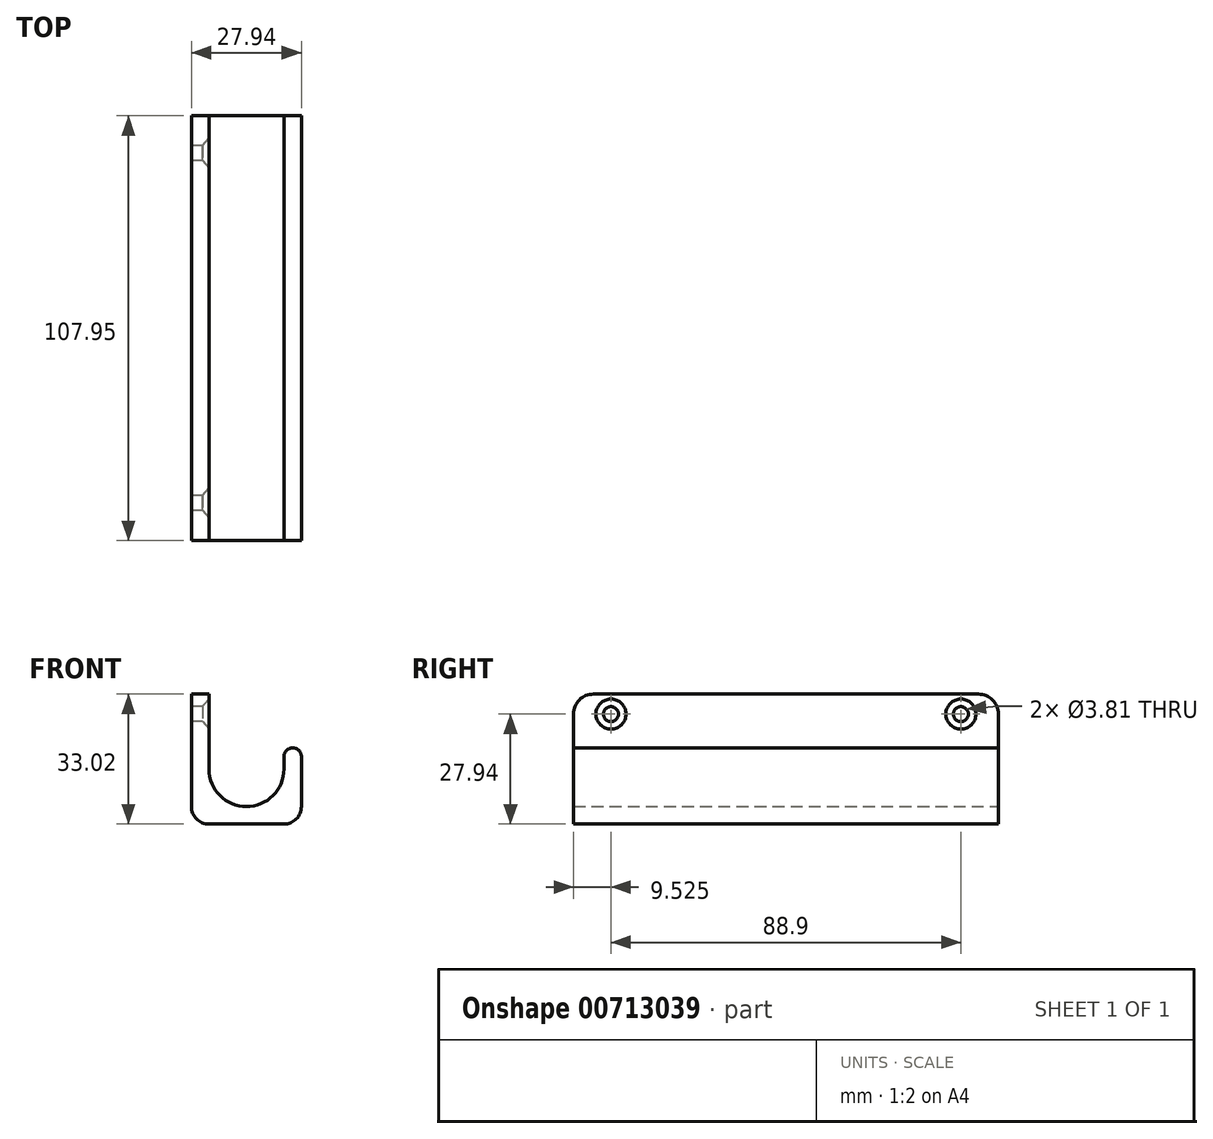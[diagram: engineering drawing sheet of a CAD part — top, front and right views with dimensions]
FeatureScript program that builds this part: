
annotation { "Feature Type Name" : "Feature", "Feature Type Description" : "" }
export const myFeature = defineFeature(function(context is Context, id is Id, definition is map)
    precondition{}
    {
        {
            var Q0;
            Q0=qCreatedBy(makeId("Front.planeOp"),FACE);
            var sketch = newSketch(context, id + "F0", { "sketchPlane" : qUnion([Q0])});
            skLineSegment(sketch, "E0", {"start": v(0, 0) * mm, "end": v(0, -28.57) * mm});
            skLineSegment(sketch, "E1", {"start": v(3.18, -31.75) * mm, "end": v(22.23, -31.75) * mm});
            skLineSegment(sketch, "E2", {"start": v(25.4, -28.57) * mm, "end": v(25.4, -15.87) * mm});
            skLineSegment(sketch, "E3", {"start": v(3.18, -19.05) * mm, "end": v(3.18, 0) * mm});
            skLineSegment(sketch, "E4", {"start": v(3.18, 0) * mm, "end": v(0, 0) * mm});
            skLineSegment(sketch, "E5", {"start": v(22.23, -15.87) * mm, "end": v(22.23, -19.05) * mm});
            skArc(sketch, "E6", {"start": v(3.18, -19.05) * mm, "mid": v(12.7, -28.58) * mm, "end": v(22.23, -19.05) * mm});
            skArc(sketch, "E7", {"start": v(22.23, -15.87) * mm, "mid": v(23.81, -14.29) * mm, "end": v(25.4, -15.87) * mm});
            skPoint(sketch, "E8.visualSharp", {"position": v(0, -31.75) * mm});
            skArc(sketch, "E8.filletArc", {"start": v(0, -28.57) * mm, "mid": v(0.93, -30.82) * mm, "end": v(3.18, -31.75) * mm});
            skPoint(sketch, "E9.visualSharp", {"position": v(25.4, -31.75) * mm});
            skArc(sketch, "E9.filletArc", {"start": v(22.23, -31.75) * mm, "mid": v(24.47, -30.82) * mm, "end": v(25.4, -28.57) * mm});
            skSolve(sketch);
        }
        {
            var Q0;
            Q0 = qSketchRegion(id + "F0", true);
            extrude(context, id + "F1", {"entities" : qUnion([Q0]), "depth" : 107.95 * mm, "offsetDistance" : 25.4 * mm});
        }
        {
            var Q0;
            Q0=makeQuery(id+"F1.opExtrude","SWEPT_FACE",FACE,{"disambiguationData":[OSD([sQuery(id+"F0.wireOp",EDGE,"E0")])]});
            var sketch = newSketch(context, id + "F2", { "sketchPlane" : qUnion([Q0])});
            skPoint(sketch, "E10.start.orphan", {"position": v(53.98, 0) * mm});
            skCircle(sketch, "E11", {"center": v(9.52, -5.08) * mm, "radius": 1.9 * mm});
            skCircle(sketch, "E12", {"center": v(98.43, -5.08) * mm, "radius": 1.9 * mm});
            skSolve(sketch);
        }
        {
            var Q0;
            Q0=makeQuery(id+"F1.opExtrude","CAP_EDGE",EDGE,{"disambiguationData":[OSD([sQuery(id+"F0.wireOp",EDGE,"E4")])],"isStart":true});
            var Q1;
            Q1=makeQuery(id+"F1.opExtrude","CAP_EDGE",EDGE,{"disambiguationData":[OSD([sQuery(id+"F0.wireOp",EDGE,"E4")])],"isStart":false});
            fillet(context, id + "F3", {"entities" : qUnion([Q0, Q1]), "radius" : 1.59 * mm, "tangentPropagation" : true, "allowEdgeOverflow" : false});
        }
        {
            var Q0;
            Q0 = qSketchRegion(id + "F2", true);
            extrude(context, id + "F4", {"entities" : qUnion([Q0]), "operationType" : NewBodyOperationType.REMOVE, "oppositeDirection" : true, "depth" : 25.4 * mm, "offsetDistance" : 25.4 * mm});
        }
        {
            var Q0;
            Q0=makeQuery(id+"F4.boolean.opBoolean","INTERSECT",EDGE,{"derivedFrom":[makeQuery(id+"F1.opExtrude","SWEPT_FACE",FACE,{"disambiguationData":[OSD([sQuery(id+"F0.wireOp",EDGE,"E3")])]}),makeQuery(id+"F4.opExtrude","SWEPT_FACE",FACE,{"disambiguationData":[OSD([sQuery(id+"F2.wireOp",EDGE,"E12")])]})]});
            var Q1;
            Q1=makeQuery(id+"F4.boolean.opBoolean","INTERSECT",EDGE,{"derivedFrom":[makeQuery(id+"F1.opExtrude","SWEPT_FACE",FACE,{"disambiguationData":[OSD([sQuery(id+"F0.wireOp",EDGE,"E3")])]}),makeQuery(id+"F4.opExtrude","SWEPT_FACE",FACE,{"disambiguationData":[OSD([sQuery(id+"F2.wireOp",EDGE,"E11")])]})]});
            chamfer(context, id + "F5", {"entities" : qUnion([Q0, Q1]), "chamferType" : ChamferType.OFFSET_ANGLE, "width" : 1.65 * mm, "oppositeDirection" : false, "angle" : 41 * degree, "tangentPropagation" : true});
        }
        {
            var Q0;
            Q0=makeQuery(id+"F1.opExtrude","CAP_FACE",FACE,{"disambiguationData":[OSD([sQuery(id+"F0.wireOp",EDGE,"E0"),sQuery(id+"F0.wireOp",EDGE,"E1"),sQuery(id+"F0.wireOp",EDGE,"E2"),sQuery(id+"F0.wireOp",EDGE,"E3"),sQuery(id+"F0.wireOp",EDGE,"E4"),sQuery(id+"F0.wireOp",EDGE,"E5"),sQuery(id+"F0.wireOp",EDGE,"E6"),sQuery(id+"F0.wireOp",EDGE,"E7"),sQuery(id+"F0.wireOp",EDGE,"E8.filletArc"),sQuery(id+"F0.wireOp",EDGE,"E9.filletArc")])],"isStart":false});
            var sketch = newSketch(context, id + "F6", { "sketchPlane" : qUnion([Q0])});
            skLineSegment(sketch, "E13.0", {"start": v(0, 0) * mm, "end": v(3.18, 0) * mm});
            skLineSegment(sketch, "E13.3", {"start": v(3.18, -19.05) * mm, "end": v(3.18, 0) * mm});
            skLineSegment(sketch, "E13.4", {"start": v(0, 0) * mm, "end": v(0, -28.57) * mm});
            skArc(sketch, "E13.5", {"start": v(3.18, -19.05) * mm, "mid": v(12.7, -28.58) * mm, "end": v(22.23, -19.05) * mm});
            skLineSegment(sketch, "E13.6", {"start": v(22.23, -15.87) * mm, "end": v(22.23, -19.05) * mm});
            skArc(sketch, "E13.7", {"start": v(22.23, -15.87) * mm, "mid": v(23.81, -14.29) * mm, "end": v(25.4, -15.87) * mm});
            skLineSegment(sketch, "E13.8", {"start": v(25.4, -28.57) * mm, "end": v(25.4, -15.87) * mm});
            skArc(sketch, "E13.9", {"start": v(22.23, -31.75) * mm, "mid": v(24.47, -30.82) * mm, "end": v(25.4, -28.57) * mm});
            skLineSegment(sketch, "E13.10", {"start": v(3.18, -31.75) * mm, "end": v(22.23, -31.75) * mm});
            skArc(sketch, "E13.11", {"start": v(0, -28.57) * mm, "mid": v(0.93, -30.82) * mm, "end": v(3.18, -31.75) * mm});
            skLineSegment(sketch, "E14.0", {"start": v(26.67, -28.57) * mm, "end": v(26.67, -15.87) * mm});
            skLineSegment(sketch, "E14.1", {"start": v(-1.27, 0) * mm, "end": v(-1.27, -28.57) * mm});
            skArc(sketch, "E14.2", {"start": v(-1.27, -28.57) * mm, "mid": v(0.03, -31.72) * mm, "end": v(3.18, -33.02) * mm});
            skLineSegment(sketch, "E14.3", {"start": v(3.18, -33.02) * mm, "end": v(22.23, -33.02) * mm});
            skArc(sketch, "E14.4", {"start": v(22.23, -33.02) * mm, "mid": v(25.37, -31.72) * mm, "end": v(26.67, -28.57) * mm});
            skArc(sketch, "E15", {"start": v(26.67, -15.87) * mm, "mid": v(24.45, -13.65) * mm, "end": v(22.23, -15.87) * mm});
            skLineSegment(sketch, "E16", {"start": v(-1.27, 0) * mm, "end": v(0, 0) * mm});
            skSolve(sketch);
        }
        {
            var Q0;
            Q0 = qSketchRegion(id + "F6", true);
            var Q1;
            Q1=makeQuery(id+"F1.opExtrude","CAP_FACE",FACE,{"disambiguationData":[OSD([sQuery(id+"F0.wireOp",EDGE,"E0"),sQuery(id+"F0.wireOp",EDGE,"E1"),sQuery(id+"F0.wireOp",EDGE,"E2"),sQuery(id+"F0.wireOp",EDGE,"E3"),sQuery(id+"F0.wireOp",EDGE,"E4"),sQuery(id+"F0.wireOp",EDGE,"E5"),sQuery(id+"F0.wireOp",EDGE,"E6"),sQuery(id+"F0.wireOp",EDGE,"E7"),sQuery(id+"F0.wireOp",EDGE,"E8.filletArc"),sQuery(id+"F0.wireOp",EDGE,"E9.filletArc")])],"isStart":true});
            extrude(context, id + "F7", {"entities" : qUnion([Q0]), "operationType" : NewBodyOperationType.ADD, "endBound" : BoundingType.UP_TO_SURFACE, "oppositeDirection" : true, "depth" : 25.4 * mm, "endBoundEntityFace" : qUnion([Q1]), "offsetDistance" : 25.4 * mm});
        }
        {
            var Q0;
            Q0=makeQuery(id+"F7.opExtrude","SWEPT_FACE",FACE,{"disambiguationData":[OSD([sQuery(id+"F6.wireOp",EDGE,"E14.1")])]});
            var sketch = newSketch(context, id + "F8", { "sketchPlane" : qUnion([Q0])});
            skPoint(sketch, "E17.0", {"position": v(53.98, 0) * mm});
            skCircle(sketch, "E17.1", {"center": v(9.52, -5.08) * mm, "radius": 1.9 * mm});
            skCircle(sketch, "E17.2", {"center": v(98.43, -5.08) * mm, "radius": 1.9 * mm});
            skSolve(sketch);
        }
        {
            var Q0;
            Q0 = qSketchRegion(id + "F8", true);
            extrude(context, id + "F9", {"entities" : qUnion([Q0]), "operationType" : NewBodyOperationType.REMOVE, "oppositeDirection" : true, "depth" : 25.4 * mm, "offsetDistance" : 25.4 * mm});
        }
        {
            var Q0;
            Q0=makeQuery(id+"F9.boolean.opBoolean","INTERSECT",EDGE,{"derivedFrom":[makeQuery(id+"F7.boolean.opBoolean","MERGE",FACE,{"derivedFrom":[makeQuery(id+"F1.opExtrude","SWEPT_FACE",FACE,{"disambiguationData":[OSD([sQuery(id+"F0.wireOp",EDGE,"E3")])]}),makeQuery(id+"F7.opExtrude","SWEPT_FACE",FACE,{"disambiguationData":[OSD([sQuery(id+"F6.wireOp",EDGE,"E13.3")])]})]}),makeQuery(id+"F9.opExtrude","SWEPT_FACE",FACE,{"disambiguationData":[OSD([sQuery(id+"F8.wireOp",EDGE,"E17.2")])]})]});
            var Q1;
            Q1=makeQuery(id+"F9.boolean.opBoolean","INTERSECT",EDGE,{"derivedFrom":[makeQuery(id+"F7.boolean.opBoolean","MERGE",FACE,{"derivedFrom":[makeQuery(id+"F1.opExtrude","SWEPT_FACE",FACE,{"disambiguationData":[OSD([sQuery(id+"F0.wireOp",EDGE,"E3")])]}),makeQuery(id+"F7.opExtrude","SWEPT_FACE",FACE,{"disambiguationData":[OSD([sQuery(id+"F6.wireOp",EDGE,"E13.3")])]})]}),makeQuery(id+"F9.opExtrude","SWEPT_FACE",FACE,{"disambiguationData":[OSD([sQuery(id+"F8.wireOp",EDGE,"E17.1")])]})]});
            chamfer(context, id + "F10", {"entities" : qUnion([Q0, Q1]), "chamferType" : ChamferType.OFFSET_ANGLE, "width" : 1.9 * mm, "oppositeDirection" : false, "angle" : 41 * degree, "tangentPropagation" : true});
        }
        {
            var Q0;
            Q0=makeQuery(id+"F7.opExtrude","CAP_EDGE",EDGE,{"disambiguationData":[OSD([sQuery(id+"F6.wireOp",EDGE,"E13.0"),sQuery(id+"F6.wireOp",EDGE,"E16")])],"isStart":true});
            var Q1;
            Q1=makeQuery(id+"F7.opExtrude","CAP_EDGE",EDGE,{"disambiguationData":[OSD([sQuery(id+"F6.wireOp",EDGE,"E13.0"),sQuery(id+"F6.wireOp",EDGE,"E16")])],"isStart":false});
            fillet(context, id + "F11", {"entities" : qUnion([Q0, Q1]), "radius" : 5.08 * mm, "tangentPropagation" : true, "allowEdgeOverflow" : false});
        }
    });
